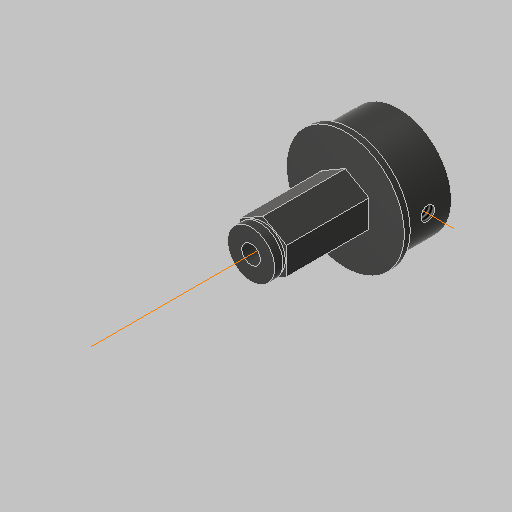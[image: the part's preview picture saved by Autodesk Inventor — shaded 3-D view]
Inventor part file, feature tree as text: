
AUTODESK INVENTOR PART (.ipt)
format: ipt  version: 2023.5 (Build 275446000, 446)  size: 203,264 bytes
history: native  units: in
note: dims shown in document units (in); Inventor stores cm internally (conversion verified against a paired STEP export)
features: extrude x5, projected_geometry x5, hole x2, plane x1, mirror x1, revolve x1, other x1
ambient origin geometry x8: Origin, YZ Plane, XZ Plane, XY Plane, X Axis, Y Axis, Z Axis, Center Point
bodies: Solid1 (feature_tree)
feature tree (16):
  extrude  "Extrusion1"  Depth=0.5in
  extrude  "Extrusion2"  Depth=1.0in TaperAngle=0.0deg
  extrude  "Extrusion3"  Depth=1.25in
  hole  "Hole1"  [1 undecoded]
  plane  "Work Plane1"
  hole  "Hole2"  [1 undecoded]
  mirror  "Mirror1"
  extrude  "Extrusion4"  Depth=0.5in TaperAngle=0.0deg
  revolve  "Revolution1"  [1 undecoded]
  extrude  "Extrusion5"  Depth=0.0125in
  other  "Work Axis1"
  projected_geometry  "Projected Loop1"
  projected_geometry  "Projected Loop2"
  projected_geometry  "Projected Loop3"
  projected_geometry  "Projected Loop4"
  projected_geometry  "Project Cut Edges1"
note: 3 required parameter values undecoded (feature->parameter linkage not recoverable at this tier; creation-order binding heuristic only, values carry confidence <= 0.55)